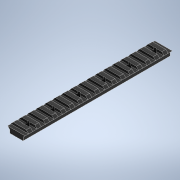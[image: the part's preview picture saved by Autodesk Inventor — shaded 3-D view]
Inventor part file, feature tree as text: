
AUTODESK INVENTOR PART (.ipt)
format: ipt  version: 2021 (Build 250183000, 183)  size: 284,160 bytes
history: native  units: mm
features: extrude x4, sketch x3, pattern_linear x2
ambient origin geometry x8: Origin, YZ Plane, XZ Plane, XY Plane, X Axis, Y Axis, Z Axis, Center Point
bodies: Solid1 (feature_tree)
feature tree (9):
  extrude  "Extrusion1"  Depth=15.67mm
  sketch  "Sketch3"  dims[d9=4.0mm d10=5.25mm d13=10.32mm d14=0.0mm d15=0.0mm d16=200.0mm d18=10.0mm d19=3.2mm d20=6.0mm d21=12.625mm d22=0.0mm d23=0.0mm d24=7.32mm d25=0.0mm d26=70.0mm d28=30.0mm]
  extrude  "Extrusion4"  Depth=174.0mm TaperAngle=0.0deg
  extrude  "Extrusion5"  Depth=5.25mm
  extrude  "Extrusion3"  Depth=30.0mm
  pattern_linear  "Rectangular Pattern1"  Spacing1=0.0mm  [1 undecoded]
  pattern_linear  "Rectangular Pattern2"  Count1=20 Spacing1=10.0mm
  sketch  "Sketch1"  dims[d0=15.67mm d1=21.21mm]
  sketch  "Sketch2"  dims[d2=3.78mm d5=174.0mm d6=0.0mm]
note: 1 required parameter value undecoded (feature->parameter linkage not recoverable at this tier; creation-order binding heuristic only, values carry confidence <= 0.55)
